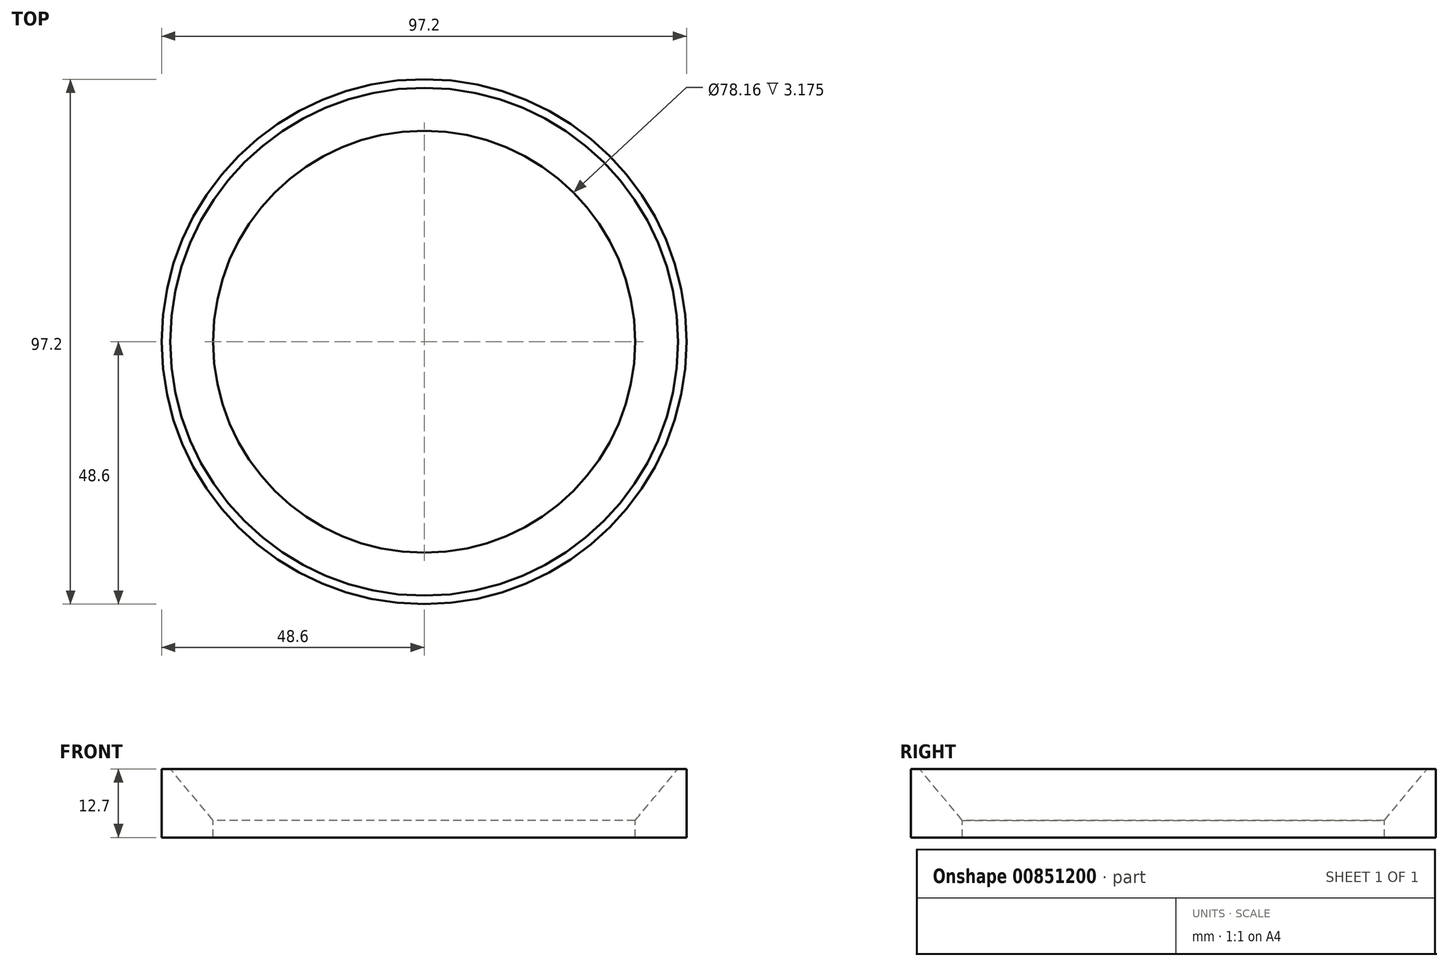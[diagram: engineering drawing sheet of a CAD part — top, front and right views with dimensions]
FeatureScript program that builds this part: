
annotation { "Feature Type Name" : "Feature", "Feature Type Description" : "" }
export const myFeature = defineFeature(function(context is Context, id is Id, definition is map)
    precondition{}
    {
        {
            var Q0;
            Q0=qCreatedBy(makeId("Front.planeOp"),FACE);
            var sketch = newSketch(context, id + "F0", { "sketchPlane" : qUnion([Q0])});
            skLineSegment(sketch, "E0", {"start": v(48.6, 0) * mm, "end": v(48.6, 12.7) * mm});
            skLineSegment(sketch, "E1", {"start": v(48.6, 12.7) * mm, "end": v(47.02, 12.7) * mm});
            skLineSegment(sketch, "E2", {"start": v(47.02, 12.7) * mm, "end": v(39.08, 3.17) * mm});
            skLineSegment(sketch, "E3", {"start": v(39.08, 3.17) * mm, "end": v(39.08, 0) * mm});
            skArc(sketch, "E4", {"start": v(44.36, 0) * mm, "mid": v(42.86, 1.06) * mm, "end": v(41.37, 0) * mm, "construction": true});
            skLineSegment(sketch, "E5", {"start": v(39.08, 0) * mm, "end": v(41.37, 0) * mm});
            skLineSegment(sketch, "E6", {"start": v(48.6, 0) * mm, "end": v(44.36, 0) * mm});
            skLineSegment(sketch, "E7", {"start": v(41.21, 1.06) * mm, "end": v(46.42, 1.06) * mm, "construction": true});
            skLineSegment(sketch, "E8", {"start": v(0, 19.6) * mm, "end": v(0, -27.09) * mm, "construction": true});
            skLineSegment(sketch, "E9", {"start": v(41.37, 0) * mm, "end": v(44.36, 0) * mm});
            skSolve(sketch);
        }
        {
            var Q0;
            Q0=makeQuery(id+"F0.imprint","IMPRINT",FACE,{"disambiguationData":[TD([[makeQuery(id+"F0.imprint","IMPRINT",EDGE,{"derivedFrom":sQuery(id+"F0.wireOp",EDGE,"E0")}),1.0]])]});
            var Q1;
            Q1=sQuery(id+"F0.wireOp",EDGE,"E8");
            revolve(context, id + "F1", {"surfaceOperationType" : NewSurfaceOperationType.NEW, "entities" : qUnion([Q0]), "axis" : qUnion([Q1]), "revolveType" : RevolveType.FULL});
        }
    });
